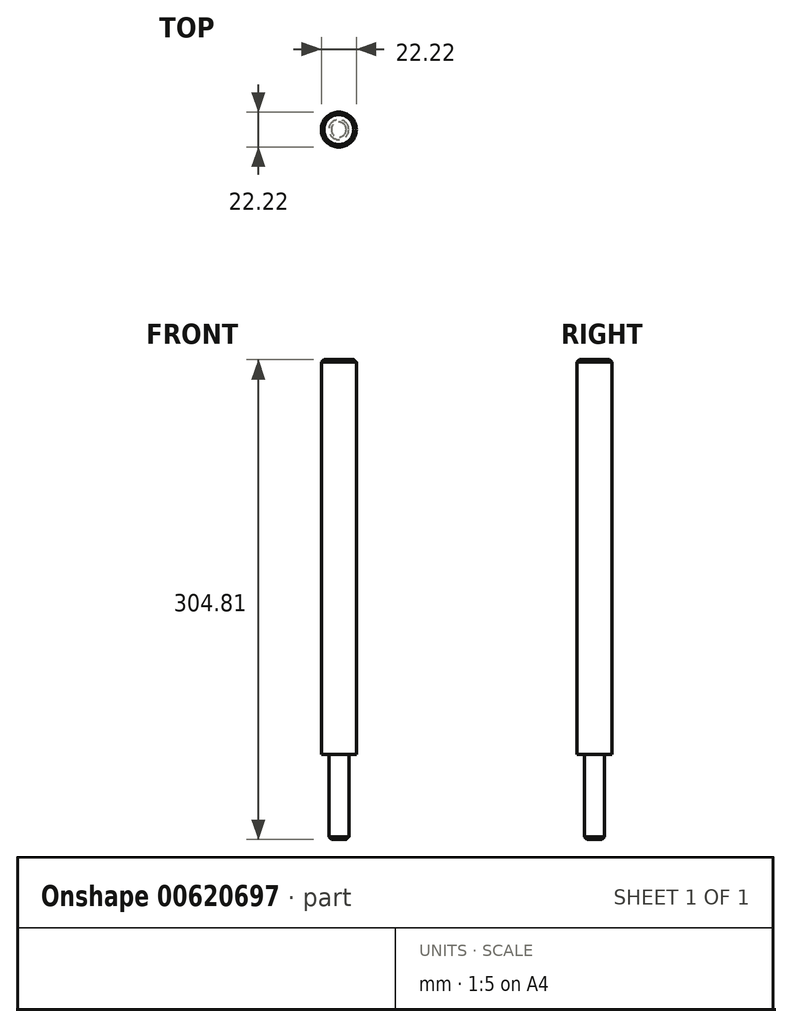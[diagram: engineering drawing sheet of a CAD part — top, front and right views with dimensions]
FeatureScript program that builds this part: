
annotation { "Feature Type Name" : "Feature", "Feature Type Description" : "" }
export const myFeature = defineFeature(function(context is Context, id is Id, definition is map)
    precondition{}
    {
        {
            var Q0;
            Q0=qCreatedBy(makeId("Top.planeOp"),FACE);
            var sketch = newSketch(context, id + "F0", { "sketchPlane" : qUnion([Q0])});
            skCircle(sketch, "E0", {"center": v(0, 0) * mm, "radius": 11.11 * mm});
            skCircle(sketch, "E1", {"center": v(0, 0) * mm, "radius": 6.35 * mm});
            skSolve(sketch);
        }
        {
            var Q0;
            Q0 = qSketchRegion(id + "F0", true);
            var Q1;
            Q1=makeQuery(id+"F0.imprint","IMPRINT",FACE,{"disambiguationData":[TD([[makeQuery(id+"F0.imprint","IMPRINT",EDGE,{"derivedFrom":sQuery(id+"F0.wireOp",EDGE,"E1")}),1.0]])]});
            extrude(context, id + "F1", {"entities" : qUnion([Q0, Q1]), "depth" : 250.82 * mm, "offsetDistance" : 25.4 * mm});
        }
        {
            var Q0;
            Q0=makeQuery(id+"F0.imprint","IMPRINT",FACE,{"disambiguationData":[TD([[makeQuery(id+"F0.imprint","IMPRINT",EDGE,{"derivedFrom":sQuery(id+"F0.wireOp",EDGE,"E1")}),1.0]])]});
            extrude(context, id + "F2", {"entities" : qUnion([Q0]), "operationType" : NewBodyOperationType.ADD, "oppositeDirection" : true, "depth" : 53.97 * mm, "offsetDistance" : 25.4 * mm});
        }
        {
            var Q0;
            Q0=makeQuery(id+"F1.opExtrude","CAP_FACE",FACE,{"disambiguationData":[OSD([sQuery(id+"F0.wireOp",EDGE,"E0")])],"isStart":false});
            var Q1;
            Q1=makeQuery(id+"F2.opExtrude","CAP_FACE",FACE,{"disambiguationData":[OSD([sQuery(id+"F0.wireOp",EDGE,"E1")])],"isStart":false});
            chamfer(context, id + "F3", {"entities" : qUnion([Q0, Q1]), "chamferType" : ChamferType.OFFSET_ANGLE, "width" : 1.59 * mm, "oppositeDirection" : false, "angle" : 45 * degree, "tangentPropagation" : true});
        }
    });
